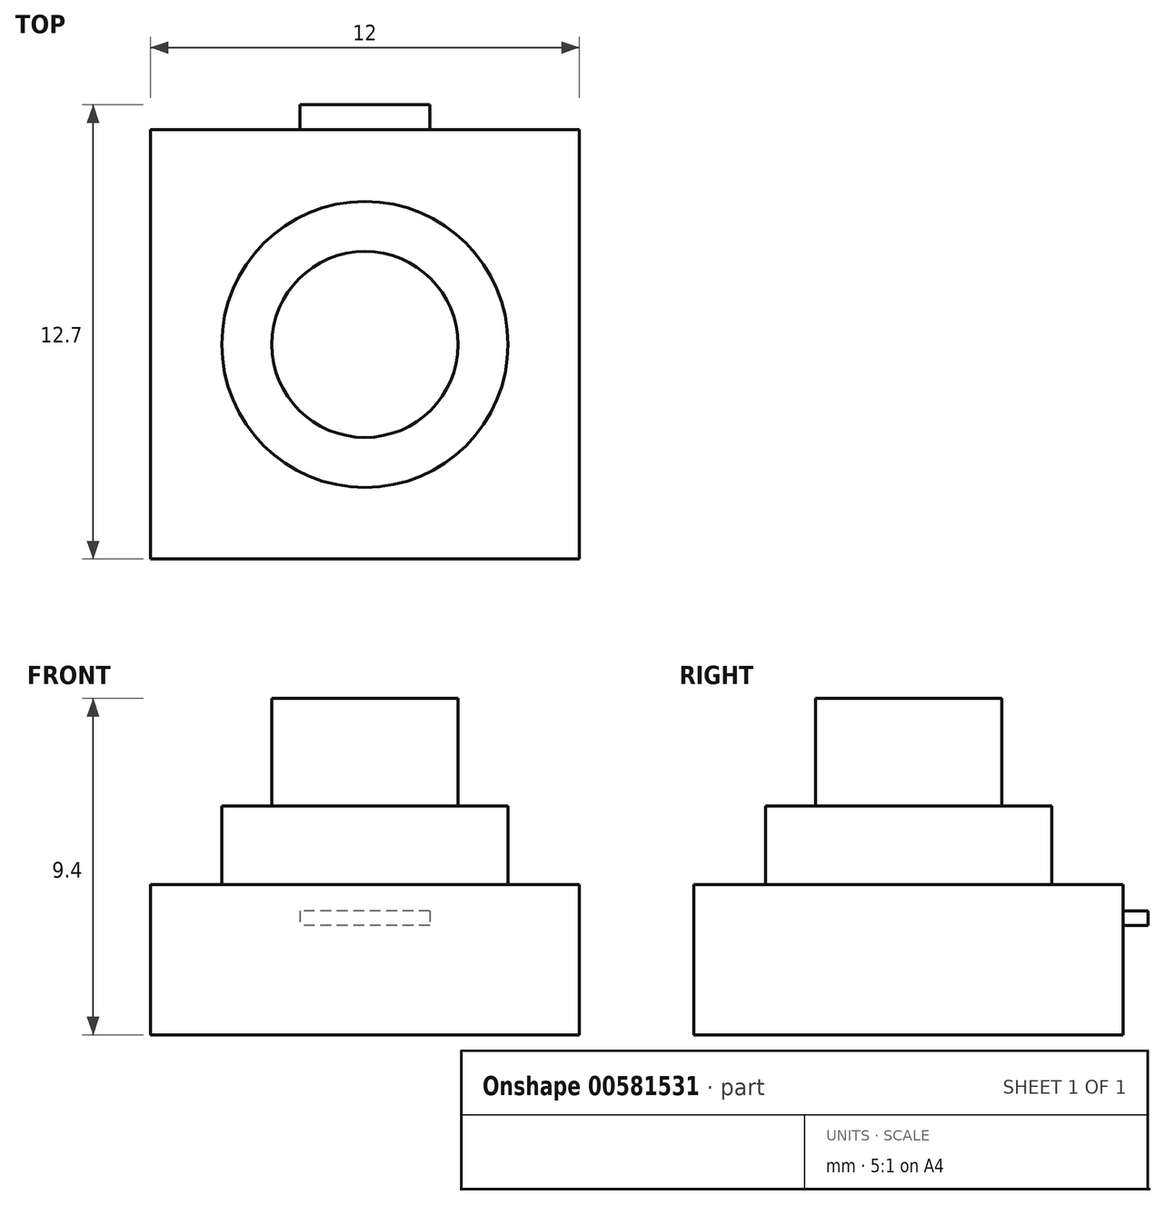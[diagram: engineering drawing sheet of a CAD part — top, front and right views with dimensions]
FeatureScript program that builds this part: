
annotation { "Feature Type Name" : "Feature", "Feature Type Description" : "" }
export const myFeature = defineFeature(function(context is Context, id is Id, definition is map)
    precondition{}
    {
        {
            var Q0;
            Q0=qCreatedBy(makeId("Top.planeOp"),FACE);
            var sketch = newSketch(context, id + "F0", { "sketchPlane" : qUnion([Q0])});
            skLineSegment(sketch, "E0.bottom", {"start": v(-6, 6) * mm, "end": v(6, 6) * mm});
            skLineSegment(sketch, "E0.top", {"start": v(-6, -6) * mm, "end": v(6, -6) * mm});
            skLineSegment(sketch, "E0.left", {"start": v(-6, 6) * mm, "end": v(-6, -6) * mm});
            skLineSegment(sketch, "E0.right", {"start": v(6, 6) * mm, "end": v(6, -6) * mm});
            skPoint(sketch, "E0.middle", {"position": v(0, 0) * mm});
            skSolve(sketch);
        }
        {
            var Q0;
            Q0 = qSketchRegion(id + "F0", true);
            extrude(context, id + "F1", {"entities" : qUnion([Q0]), "depth" : 4.2 * mm, "offsetDistance" : 25 * mm});
        }
        {
            var Q0;
            Q0=makeQuery(id+"F1.opExtrude","CAP_FACE",FACE,{"disambiguationData":[OSD([sQuery(id+"F0.wireOp",EDGE,"E0.bottom"),sQuery(id+"F0.wireOp",EDGE,"E0.top"),sQuery(id+"F0.wireOp",EDGE,"E0.left"),sQuery(id+"F0.wireOp",EDGE,"E0.right")])],"isStart":false});
            var sketch = newSketch(context, id + "F2", { "sketchPlane" : qUnion([Q0])});
            skCircle(sketch, "E1", {"center": v(0, 0) * mm, "radius": 4 * mm});
            skSolve(sketch);
        }
        {
            var Q0;
            Q0 = qSketchRegion(id + "F2", true);
            extrude(context, id + "F3", {"entities" : qUnion([Q0]), "operationType" : NewBodyOperationType.ADD, "depth" : 2.2 * mm, "offsetDistance" : 25 * mm});
        }
        {
            var Q0;
            Q0=makeQuery(id+"F3.opExtrude","CAP_FACE",FACE,{"disambiguationData":[OSD([sQuery(id+"F2.wireOp",EDGE,"E1")])],"isStart":false});
            var sketch = newSketch(context, id + "F4", { "sketchPlane" : qUnion([Q0])});
            skCircle(sketch, "E2", {"center": v(0, 0) * mm, "radius": 2.6 * mm});
            skSolve(sketch);
        }
        {
            var Q0;
            Q0 = qSketchRegion(id + "F4", true);
            extrude(context, id + "F5", {"entities" : qUnion([Q0]), "operationType" : NewBodyOperationType.ADD, "depth" : 3 * mm, "offsetDistance" : 25 * mm});
        }
        {
            var Q0;
            Q0=makeQuery(id+"F1.opExtrude","SWEPT_FACE",FACE,{"disambiguationData":[OSD([sQuery(id+"F0.wireOp",EDGE,"E0.bottom")])]});
            var sketch = newSketch(context, id + "F6", { "sketchPlane" : qUnion([Q0])});
            skLineSegment(sketch, "E3.bottom", {"start": v(-1.82, 3.46) * mm, "end": v(1.82, 3.46) * mm});
            skLineSegment(sketch, "E3.top", {"start": v(-1.82, 3.06) * mm, "end": v(1.82, 3.06) * mm});
            skLineSegment(sketch, "E3.left", {"start": v(-1.82, 3.46) * mm, "end": v(-1.82, 3.06) * mm});
            skLineSegment(sketch, "E3.right", {"start": v(1.82, 3.46) * mm, "end": v(1.82, 3.06) * mm});
            skPoint(sketch, "E3.middle", {"position": v(0, 3.26) * mm});
            skPoint(sketch, "E3.middle.positionSnap0", {"position": v(0, 4.2) * mm});
            skPoint(sketch, "E3.centerSnap0", {"position": v(0, 4.2) * mm});
            skSolve(sketch);
        }
        {
            var Q0;
            Q0 = qSketchRegion(id + "F6", true);
            extrude(context, id + "F7", {"entities" : qUnion([Q0]), "operationType" : NewBodyOperationType.ADD, "depth" : 0.7 * mm, "offsetDistance" : 25 * mm});
        }
    });
